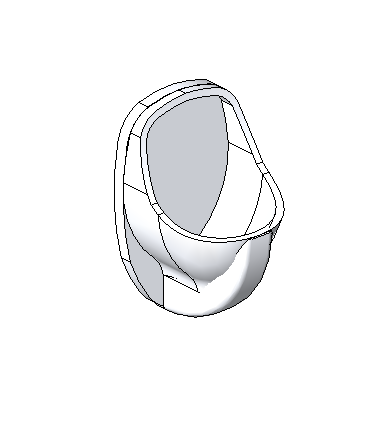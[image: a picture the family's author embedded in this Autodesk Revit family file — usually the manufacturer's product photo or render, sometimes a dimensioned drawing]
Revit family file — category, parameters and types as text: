
# Revit family: Deca_Mictório_M.714_Válvula EmbutidaFFFFF
name_source: partatom
category: Plumbing Fixtures
revit_build: Autodesk Revit Architecture 2012 (Build: 20120126_0600(x64)
units: mm (PartAtom-declared; Revit-internal decimal feet)

## types (1)
- M.714_Branco Gelo GE17
    Aprovado por = Contino/quattroD
    Assembly Code = D2010200
    Atendimento ao Cliente = 0800-0117073
    CWFU = 0
    Criado por = Contino/quattroD
    Código = M.714
    Default Elevation = 700 mm  [stored 2.29659 ft]
    Description = Mictório
    Diâmetro Ponto de Agua = 15 mm  [stored 0.0492126 ft]
    Diâmetro Ponto de Esgoto = 50 mm  [stored 0.164042 ft]
    Flow Pressure = 0.00 psi
    Informações Complementares = Sifão integrado Altura recomendada de ponto de esgoto: 520 mm Utilizar com Decalux embutido 2780 c
    Linha = Mictórios
    Louça/Metais = Louça
    Manufacturer = Deca
    Material = Deca_Vitreous China
    Mictorio = Deca GE17 Branco Gelo Cerâmica
    Model = M.714
    Norma = ABNT NBR 15097-1: 2011 / ABNT NBR 15097-2: 2011
    Peso Liquido (Kg) = 18.85
    Produto = Mictório para Válvula Embutida
    Raio Ponto de Agua = 8 mm  [stored 0.0262467 ft]
    Raio Ponto de Esgoto = 25 mm  [stored 0.082021 ft]
    Segmento = Médio
    URL = www.deca.com.br/produtos
    Variações de COR = Branco (M.714).
    Vendido Separadamente = Conjunto para instalação do mictório M714: (FM.714.01).
    WFU = 0

note: [stored X ft] marks values corroborated as IEEE doubles in the binary element streams (Revit-internal decimal feet)

## geometry (parser evidence)
native form markers: Blend x4, Sweep x2
no freeform markers — native parametric forms only
